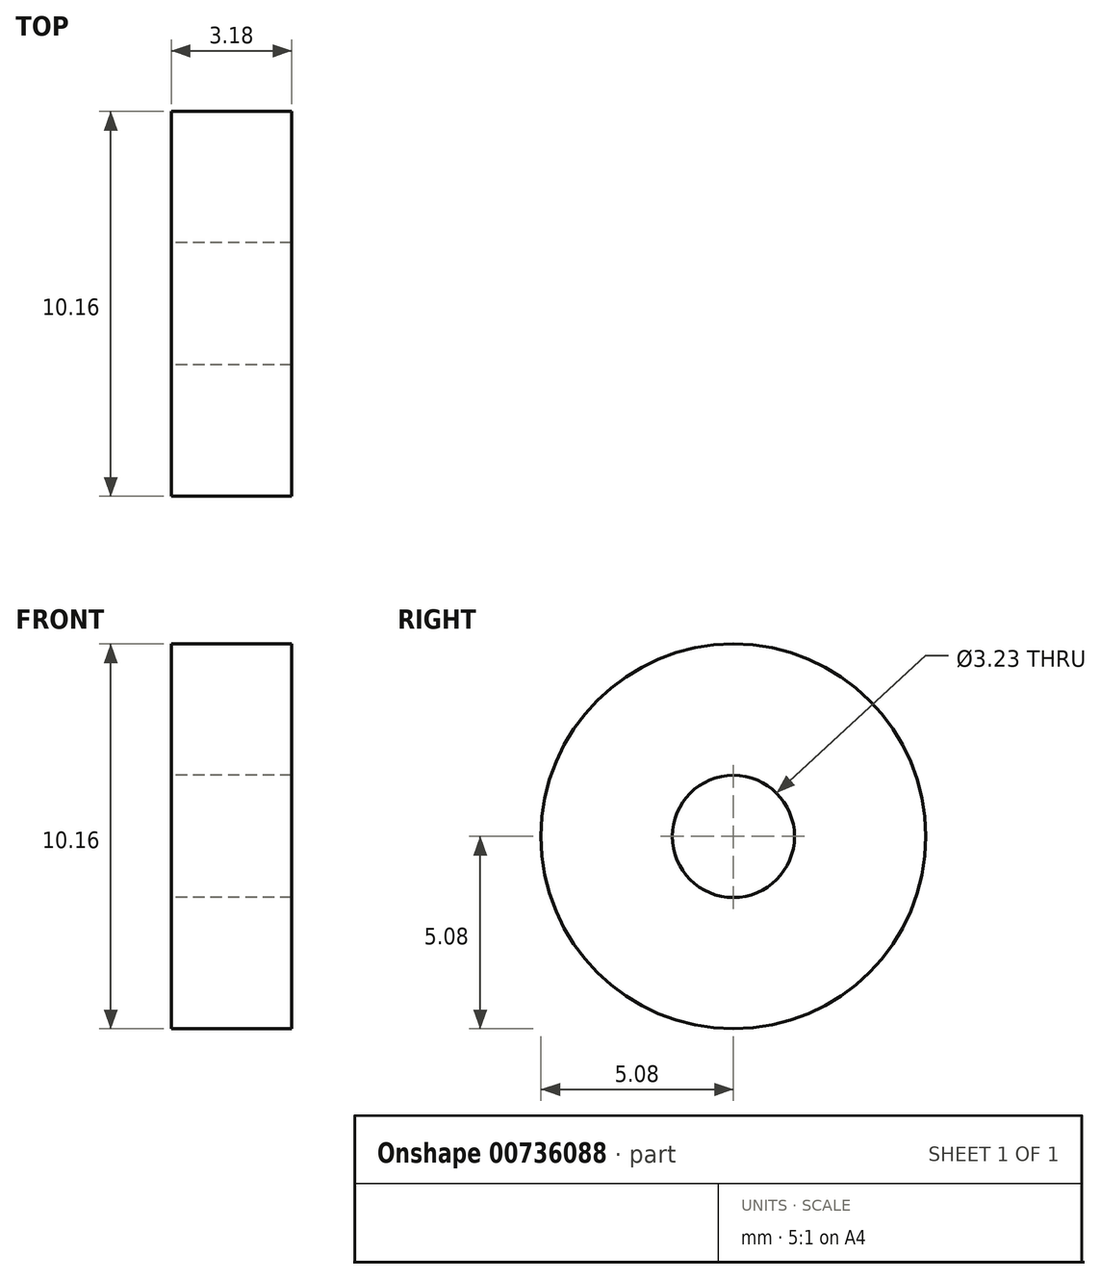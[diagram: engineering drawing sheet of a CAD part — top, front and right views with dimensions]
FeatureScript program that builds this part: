
annotation { "Feature Type Name" : "Feature", "Feature Type Description" : "" }
export const myFeature = defineFeature(function(context is Context, id is Id, definition is map)
    precondition{}
    {
        {
            var Q0;
            Q0=qCreatedBy(makeId("Right.planeOp"),FACE);
            var sketch = newSketch(context, id + "F0", { "sketchPlane" : qUnion([Q0])});
            skCircle(sketch, "E0", {"center": v(0, 0) * mm, "radius": 1.61 * mm});
            skCircle(sketch, "E1", {"center": v(0, 0) * mm, "radius": 5.08 * mm});
            skSolve(sketch);
        }
        {
            var Q0;
            Q0=makeQuery(id+"F0.imprint","IMPRINT",FACE,{"disambiguationData":[TD([[makeQuery(id+"F0.imprint","IMPRINT",EDGE,{"derivedFrom":sQuery(id+"F0.wireOp",EDGE,"E0")}),-1.0]])]});
            extrude(context, id + "F1", {"entities" : qUnion([Q0]), "depth" : 3.17 * mm, "offsetDistance" : 25.4 * mm});
        }
    });
